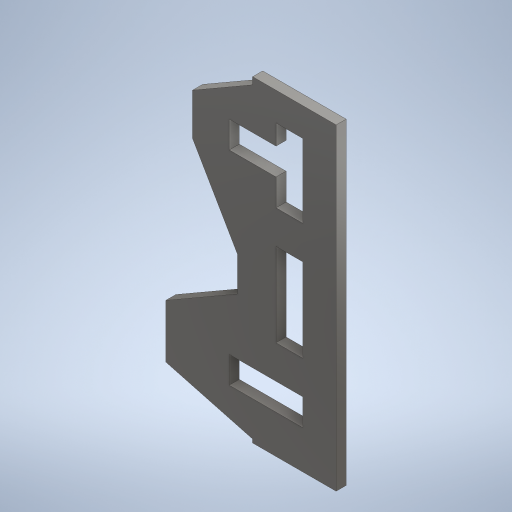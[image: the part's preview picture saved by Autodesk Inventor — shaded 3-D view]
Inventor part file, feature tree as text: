
AUTODESK INVENTOR PART (.ipt)
format: ipt  version: 2024 (Build 280153000, 153)  size: 282,112 bytes
history: native  units: mm
features: extrude x1, sketch x1
ambient origin geometry x8: Origin, YZ Plane, XZ Plane, XY Plane, X Axis, Y Axis, Z Axis, Center Point
bodies: Solid1 (feature_tree)
feature tree (2):
  extrude  "Extrusion1"  Depth=6.0mm
  sketch  "Sketch1"  dims[d2=25.0mm d3=25.0mm d4=92.0mm d5=32.0mm d6=16.0mm d10=35.326478mm d13=15.0deg d14=150.0deg d15=120.0deg d16=16.0mm d17=12.0mm d18=28.0mm d19=17.0mm d20=44.0mm d21=20.0mm d22=50.0mm d24=16.0mm d25=20.0mm d26=16.0mm d27=44.0mm d36=43.0mm d37=120.0deg d38=86.0mm d39=50.0mm d40=14.72219mm d41=102.0mm d42=50.0mm d43=20.0mm d44=6.0mm d45=0.0mm]
